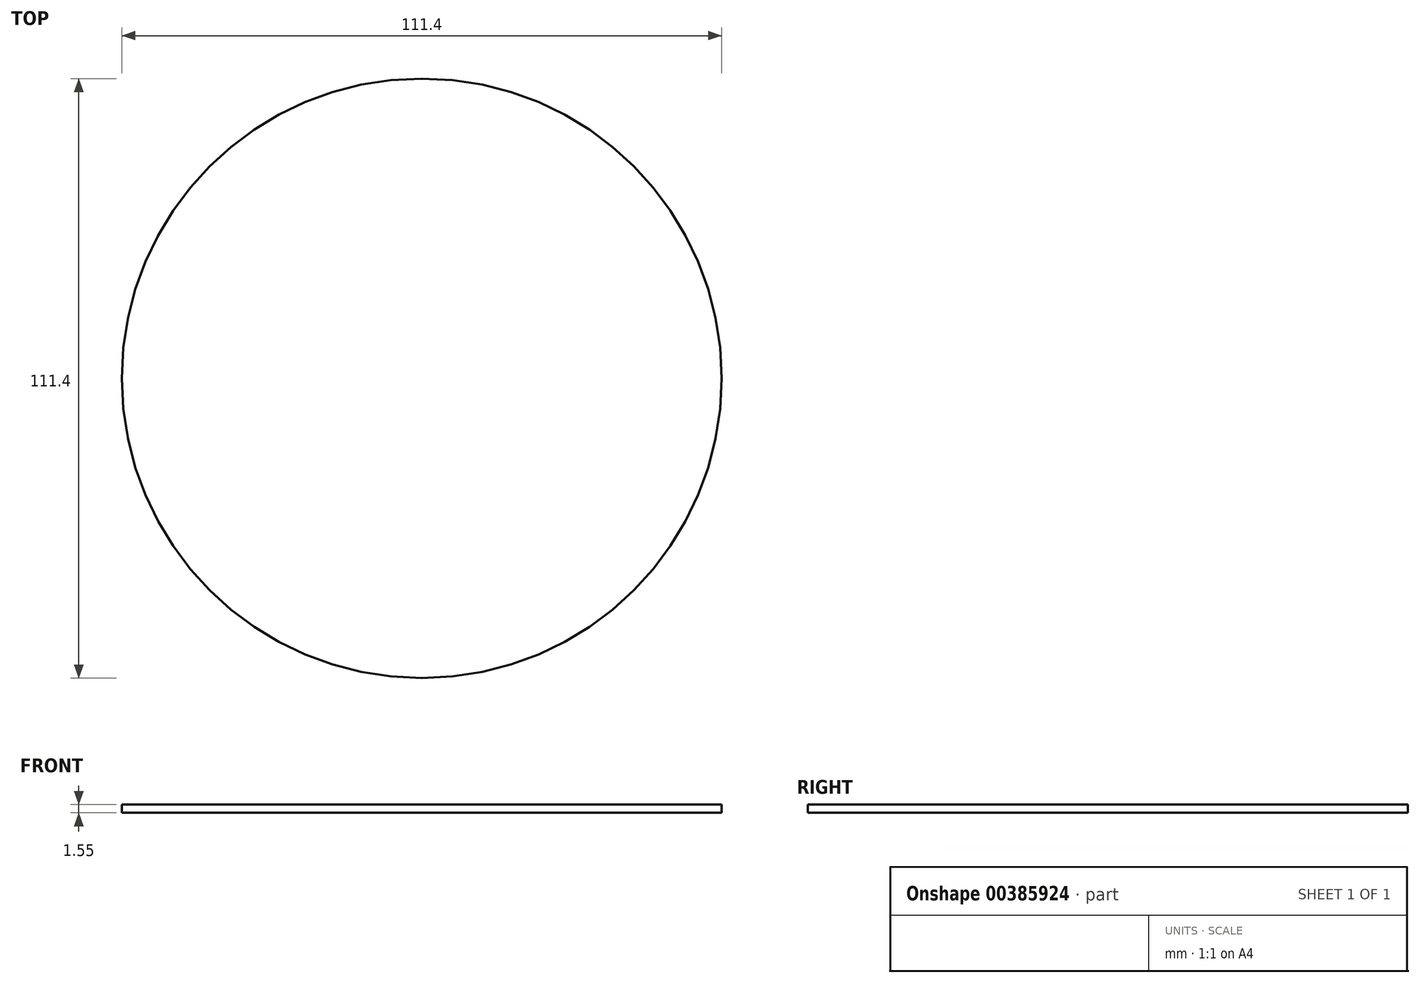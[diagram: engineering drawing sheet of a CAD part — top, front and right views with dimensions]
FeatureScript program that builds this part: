
annotation { "Feature Type Name" : "Feature", "Feature Type Description" : "" }
export const myFeature = defineFeature(function(context is Context, id is Id, definition is map)
    precondition{}
    {
        {
            var Q0;
            Q0=qCreatedBy(makeId("Top.planeOp"),FACE);
            var sketch = newSketch(context, id + "F0", { "sketchPlane" : qUnion([Q0])});
            skCircle(sketch, "E0", {"center": v(0, 0) * mm, "radius": 55.7 * mm});
            skSolve(sketch);
        }
        {
            var Q0;
            Q0 = qSketchRegion(id + "F0", true);
            extrude(context, id + "F1", {"entities" : qUnion([Q0]), "depth" : 1.55 * mm});
        }
    });
